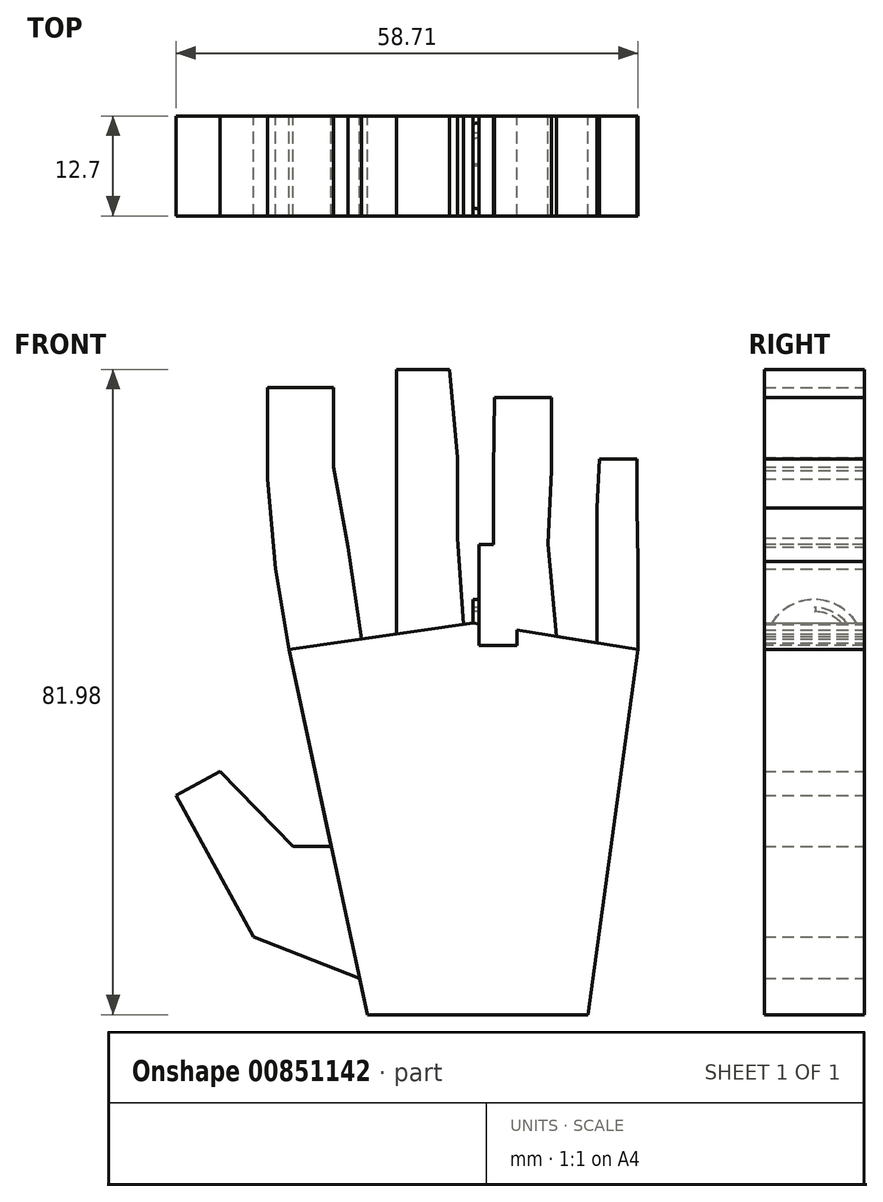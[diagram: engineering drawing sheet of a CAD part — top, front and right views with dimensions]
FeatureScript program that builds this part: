
annotation { "Feature Type Name" : "Feature", "Feature Type Description" : "" }
export const myFeature = defineFeature(function(context is Context, id is Id, definition is map)
    precondition{}
    {
        {
            var Q0;
            Q0=qCreatedBy(makeId("Front.planeOp"),FACE);
            var sketch = newSketch(context, id + "F0", { "sketchPlane" : qUnion([Q0])});
            skLineSegment(sketch, "E0", {"start": v(14.62, -41.57) * mm, "end": v(-13.4, -41.57) * mm});
            skPoint(sketch, "E1.orphan", {"position": v(0, -41.57) * mm});
            skLineSegment(sketch, "E2", {"start": v(-13.4, -41.57) * mm, "end": v(-23.39, 4.81) * mm});
            skLineSegment(sketch, "E3", {"start": v(-23.39, 4.81) * mm, "end": v(0, 8.2) * mm});
            skLineSegment(sketch, "E4", {"start": v(0, 8.2) * mm, "end": v(20.98, 4.81) * mm});
            skLineSegment(sketch, "E5", {"start": v(14.62, -41.57) * mm, "end": v(20.98, 4.81) * mm});
            skLineSegment(sketch, "E6", {"start": v(-14.4, -36.97) * mm, "end": v(-27.9, -31.67) * mm});
            skLineSegment(sketch, "E7", {"start": v(-27.9, -31.67) * mm, "end": v(-37.73, -13.72) * mm});
            skLineSegment(sketch, "E8", {"start": v(-37.73, -13.72) * mm, "end": v(-32.12, -10.65) * mm});
            skLineSegment(sketch, "E9", {"start": v(-32.12, -10.65) * mm, "end": v(-22.87, -20.16) * mm});
            skLineSegment(sketch, "E10", {"start": v(-22.87, -20.16) * mm, "end": v(-18.01, -20.16) * mm});
            skLineSegment(sketch, "E11", {"start": v(-23.39, 4.81) * mm, "end": v(-25.12, 15.03) * mm});
            skLineSegment(sketch, "E12", {"start": v(-25.12, 15.03) * mm, "end": v(-26.13, 26.5) * mm});
            skLineSegment(sketch, "E13", {"start": v(-26.13, 26.5) * mm, "end": v(-26.13, 38.07) * mm});
            skLineSegment(sketch, "E14", {"start": v(-26.13, 38.07) * mm, "end": v(-17.7, 38.07) * mm});
            skLineSegment(sketch, "E15", {"start": v(-17.7, 38.07) * mm, "end": v(-17.7, 28.01) * mm});
            skLineSegment(sketch, "E16", {"start": v(-17.7, 28.01) * mm, "end": v(-26.13, 26.5) * mm});
            skLineSegment(sketch, "E17", {"start": v(-17.7, 28.01) * mm, "end": v(-15.87, 17.87) * mm});
            skLineSegment(sketch, "E18", {"start": v(-15.87, 17.87) * mm, "end": v(-25.12, 15.03) * mm});
            skLineSegment(sketch, "E19", {"start": v(-15.87, 17.87) * mm, "end": v(-14.17, 6.15) * mm});
            skLineSegment(sketch, "E20", {"start": v(-9.7, 6.8) * mm, "end": v(-9.7, 18.15) * mm});
            skLineSegment(sketch, "E21", {"start": v(-9.7, 18.15) * mm, "end": v(-9.7, 29.23) * mm});
            skLineSegment(sketch, "E22", {"start": v(-9.7, 29.23) * mm, "end": v(-1.96, 29.23) * mm});
            skLineSegment(sketch, "E23", {"start": v(-1.96, 29.23) * mm, "end": v(-1.96, 18.96) * mm});
            skLineSegment(sketch, "E24", {"start": v(-1.96, 18.96) * mm, "end": v(-1.21, 8.03) * mm});
            skLineSegment(sketch, "E25", {"start": v(-9.7, 29.23) * mm, "end": v(-9.7, 40.4) * mm});
            skLineSegment(sketch, "E26", {"start": v(-9.7, 40.4) * mm, "end": v(-3.03, 40.4) * mm});
            skLineSegment(sketch, "E27", {"start": v(-3.03, 40.4) * mm, "end": v(-1.96, 29.23) * mm});
            skLineSegment(sketch, "E28", {"start": v(-9.7, 18.15) * mm, "end": v(-1.96, 18.96) * mm});
            skLineSegment(sketch, "E29", {"start": v(2.62, 7.78) * mm, "end": v(2.62, 18.22) * mm});
            skLineSegment(sketch, "E30", {"start": v(2.62, 18.22) * mm, "end": v(9.49, 18.22) * mm});
            skLineSegment(sketch, "E31", {"start": v(9.49, 18.22) * mm, "end": v(10.58, 6.5) * mm});
            skLineSegment(sketch, "E32", {"start": v(10.58, 6.5) * mm, "end": v(9.49, 18.22) * mm});
            skLineSegment(sketch, "E33", {"start": v(2.62, 18.22) * mm, "end": v(2.62, 27.54) * mm});
            skLineSegment(sketch, "E34", {"start": v(2.62, 27.54) * mm, "end": v(9.95, 27.54) * mm});
            skLineSegment(sketch, "E35", {"start": v(9.95, 27.54) * mm, "end": v(9.49, 18.22) * mm});
            skLineSegment(sketch, "E36", {"start": v(9.95, 27.54) * mm, "end": v(9.95, 36.85) * mm});
            skLineSegment(sketch, "E37", {"start": v(9.95, 36.85) * mm, "end": v(2.7, 36.85) * mm});
            skLineSegment(sketch, "E38", {"start": v(2.7, 36.85) * mm, "end": v(2.62, 27.54) * mm});
            skLineSegment(sketch, "E39", {"start": v(20.98, 4.81) * mm, "end": v(20.98, 15.98) * mm});
            skLineSegment(sketch, "E40", {"start": v(20.98, 15.98) * mm, "end": v(15.71, 15.98) * mm});
            skLineSegment(sketch, "E41", {"start": v(15.71, 15.98) * mm, "end": v(15.71, 5.66) * mm});
            skLineSegment(sketch, "E42", {"start": v(15.71, 15.98) * mm, "end": v(15.71, 22.79) * mm});
            skLineSegment(sketch, "E43", {"start": v(15.71, 22.79) * mm, "end": v(20.79, 22.79) * mm});
            skLineSegment(sketch, "E44", {"start": v(20.79, 22.79) * mm, "end": v(20.98, 15.98) * mm});
            skLineSegment(sketch, "E45", {"start": v(20.79, 22.79) * mm, "end": v(20.79, 29.03) * mm});
            skLineSegment(sketch, "E46", {"start": v(20.79, 29.03) * mm, "end": v(16.05, 29.03) * mm});
            skLineSegment(sketch, "E47", {"start": v(16.05, 29.03) * mm, "end": v(15.71, 22.79) * mm});
            skLineSegment(sketch, "E48", {"start": v(-18.77, 5.48) * mm, "end": v(-9.34, -41.57) * mm, "construction": true});
            skLineSegment(sketch, "E49", {"start": v(-5.64, 7.38) * mm, "end": v(-4.1, -41.57) * mm, "construction": true});
            skLineSegment(sketch, "E50", {"start": v(6.52, 7.15) * mm, "end": v(4.6, -41.57) * mm, "construction": true});
            skLineSegment(sketch, "E51", {"start": v(18.1, 5.28) * mm, "end": v(11.7, -41.57) * mm, "construction": true});
            skSolve(sketch);
        }
        {
            var Q0;
            Q0 = qSketchRegion(id + "F0", true);
            extrude(context, id + "F1", {"entities" : qUnion([Q0]), "endBound" : BoundingType.SYMMETRIC, "depth" : 12.7 * mm, "offsetDistance" : 25.4 * mm});
        }
        {
            var Q0;
            Q0=qCreatedBy(makeId("Front.planeOp"),FACE);
            var sketch = newSketch(context, id + "F2", { "sketchPlane" : qUnion([Q0])});
            skLineSegment(sketch, "E52.0", {"start": v(-13.4, -41.57) * mm, "end": v(-23.39, 4.81) * mm});
            skLineSegment(sketch, "E53.0", {"start": v(14.62, -41.57) * mm, "end": v(-13.4, -41.57) * mm});
            skLineSegment(sketch, "E54.0", {"start": v(14.62, -41.57) * mm, "end": v(20.98, 4.81) * mm});
            skLineSegment(sketch, "E55.0", {"start": v(0, 8.2) * mm, "end": v(20.98, 4.81) * mm});
            skLineSegment(sketch, "E56.0", {"start": v(-23.39, 4.81) * mm, "end": v(0, 8.2) * mm});
            skSolve(sketch);
        }
        {
            var Q0;
            Q0 = qSketchRegion(id + "F2", true);
            extrude(context, id + "F3", {"entities" : qUnion([Q0]), "endBound" : BoundingType.SYMMETRIC, "depth" : 12.7 * mm, "offsetDistance" : 25.4 * mm});
        }
        {
            var Q0;
            Q0=qCreatedBy(makeId("Right.planeOp"),FACE);
            var sketch = newSketch(context, id + "F4", { "sketchPlane" : qUnion([Q0])});
            skLineSegment(sketch, "E57", {"start": v(6.35, 4.81) * mm, "end": v(-6.35, 4.81) * mm});
            skPoint(sketch, "E58.orphan", {"position": v(0, 4.81) * mm});
            skArc(sketch, "E59", {"start": v(6.35, 4.81) * mm, "mid": v(0, 11.16) * mm, "end": v(-6.35, 4.81) * mm});
            skArc(sketch, "E60", {"start": v(5.33, 4.81) * mm, "mid": v(3.77, 8.58) * mm, "end": v(0, 10.15) * mm});
            skArc(sketch, "E61", {"start": v(4.83, 4.81) * mm, "mid": v(3.41, 8.23) * mm, "end": v(0, 9.64) * mm});
            skArc(sketch, "E62", {"start": v(0, 10.15) * mm, "mid": v(-0.25, 9.9) * mm, "end": v(0, 9.64) * mm});
            skLineSegment(sketch, "E63", {"start": v(-6.33, 5.32) * mm, "end": v(6.33, 5.32) * mm});
            skPoint(sketch, "E64.orphan", {"position": v(0, 5.32) * mm});
            skSolve(sketch);
        }
        {
            var Q0;
            {var subQ0=sQuery(id+"F4.wireOp",EDGE,"E59");var subQ1=sQuery(id+"F4.wireOp",EDGE,"E57");var subQ2=makeQuery(id+"F4.imprint","INTERSECT",VERTEX,{"disambiguationData":[OD(1.0)],"derivedFrom":[subQ1,subQ0]});Q0=makeQuery(id+"F4.imprint","IMPRINT",FACE,{"disambiguationData":[TD([[makeQuery(id+"F4.imprint","IMPRINT",EDGE,{"disambiguationData":[TD([[subQ2,1.0]])],"derivedFrom":subQ1}),-1.0]])]});}
            var Q1;
            {var subQ0=sQuery(id+"F4.wireOp",EDGE,"E60");var subQ1=sQuery(id+"F4.wireOp",EDGE,"E57");var subQ2=makeQuery(id+"F4.imprint","INTERSECT",VERTEX,{"derivedFrom":[subQ1,subQ0]});Q1=makeQuery(id+"F4.imprint","IMPRINT",FACE,{"disambiguationData":[TD([[makeQuery(id+"F4.imprint","IMPRINT",EDGE,{"disambiguationData":[TD([[subQ2,-1.0]])],"derivedFrom":subQ1}),-1.0]])]});}
            var Q2;
            {var subQ0=sQuery(id+"F4.wireOp",EDGE,"E59");var subQ1=sQuery(id+"F4.wireOp",EDGE,"E57");var subQ2=makeQuery(id+"F4.imprint","INTERSECT",VERTEX,{"disambiguationData":[OD(0.0)],"derivedFrom":[subQ1,subQ0]});Q2=makeQuery(id+"F4.imprint","IMPRINT",FACE,{"disambiguationData":[TD([[makeQuery(id+"F4.imprint","IMPRINT",EDGE,{"disambiguationData":[TD([[subQ2,-1.0]])],"derivedFrom":subQ1}),-1.0]])]});}
            var Q3;
            {var subQ0=sQuery(id+"F4.wireOp",EDGE,"E62");Q3=makeQuery(id+"F4.imprint","IMPRINT",FACE,{"disambiguationData":[TD([[makeQuery(id+"F4.imprint","IMPRINT",EDGE,{"derivedFrom":subQ0}),-1.0]])]});}
            extrude(context, id + "F5", {"entities" : qUnion([Q0, Q1, Q2, Q3]), "depth" : 6.35 * mm, "offsetDistance" : 25.4 * mm});
        }
        {
            var Q0;
            Q0=qCreatedBy(makeId("Front.planeOp"),FACE);
            var sketch = newSketch(context, id + "F6", { "sketchPlane" : qUnion([Q0])});
            skLineSegment(sketch, "E65.bottom", {"start": v(5.59, 5.32) * mm, "end": v(0.76, 5.32) * mm});
            skLineSegment(sketch, "E65.top", {"start": v(5.59, 11.97) * mm, "end": v(0.76, 11.97) * mm});
            skLineSegment(sketch, "E65.left", {"start": v(5.59, 5.32) * mm, "end": v(5.59, 11.97) * mm});
            skLineSegment(sketch, "E65.right", {"start": v(0.76, 5.32) * mm, "end": v(0.76, 11.97) * mm});
            skSolve(sketch);
        }
        {
            var Q0;
            Q0 = qSketchRegion(id + "F6", true);
            extrude(context, id + "F7", {"entities" : qUnion([Q0]), "operationType" : NewBodyOperationType.REMOVE, "endBound" : BoundingType.THROUGH_ALL, "oppositeDirection" : true, "depth" : 25.4 * mm, "offsetDistance" : 25.4 * mm, "hasSecondDirection" : true, "secondDirectionBound" : SecondDirectionBoundingType.THROUGH_ALL, "secondDirectionOppositeDirection" : false, "secondDirectionDepth" : 25.4 * mm});
        }
        {
            var Q0;
            Q0=qCreatedBy(makeId("Front.planeOp"),FACE);
            var sketch = newSketch(context, id + "F8", { "sketchPlane" : qUnion([Q0])});
            skLineSegment(sketch, "E66", {"start": v(5.59, 5.32) * mm, "end": v(0.76, 5.32) * mm});
            skLineSegment(sketch, "E67", {"start": v(0.76, 5.32) * mm, "end": v(0.76, 18.15) * mm});
            skLineSegment(sketch, "E68", {"start": v(5.59, 5.32) * mm, "end": v(5.59, 18.15) * mm});
            skLineSegment(sketch, "E69", {"start": v(5.59, 18.15) * mm, "end": v(0.76, 18.15) * mm});
            skLineSegment(sketch, "E70", {"start": v(0.76, 10.15) * mm, "end": v(0, 10.15) * mm});
            skLineSegment(sketch, "E71", {"start": v(0.76, 9.64) * mm, "end": v(0, 9.64) * mm});
            skLineSegment(sketch, "E72", {"start": v(0, 9.64) * mm, "end": v(0, 10.15) * mm});
            skLineSegment(sketch, "E73", {"start": v(5.59, 10.15) * mm, "end": v(6.35, 10.15) * mm});
            skLineSegment(sketch, "E74", {"start": v(6.35, 10.15) * mm, "end": v(6.35, 9.64) * mm});
            skLineSegment(sketch, "E75", {"start": v(6.35, 9.64) * mm, "end": v(5.59, 9.64) * mm});
            skLineSegment(sketch, "E76", {"start": v(0, 9.9) * mm, "end": v(0.76, 9.9) * mm});
            skLineSegment(sketch, "E77", {"start": v(6.35, 9.9) * mm, "end": v(5.59, 9.9) * mm});
            skSolve(sketch);
        }
        {
            var Q0;
            {var subQ4=sQuery(id+"F8.wireOp",EDGE,"E66");Q0=makeQuery(id+"F8.imprint","IMPRINT",FACE,{"disambiguationData":[TD([[makeQuery(id+"F8.imprint","IMPRINT",EDGE,{"derivedFrom":subQ4}),-1.0]])]});}
            extrude(context, id + "F9", {"entities" : qUnion([Q0]), "endBound" : BoundingType.SYMMETRIC, "depth" : 12.7 * mm, "offsetDistance" : 25.4 * mm});
        }
        {
            var Q0;
            {var subQ0=sQuery(id+"F8.wireOp",EDGE,"E73");Q0=makeQuery(id+"F8.imprint","IMPRINT",FACE,{"disambiguationData":[TD([[makeQuery(id+"F8.imprint","IMPRINT",EDGE,{"derivedFrom":subQ0}),-1.0]])]});}
            var Q1;
            Q1=sQuery(id+"F8.wireOp",EDGE,"E77");
            revolve(context, id + "F10", {"operationType" : NewBodyOperationType.ADD, "surfaceOperationType" : NewSurfaceOperationType.NEW, "entities" : qUnion([Q0]), "axis" : qUnion([Q1]), "revolveType" : RevolveType.FULL});
        }
        {
            var Q0;
            {var subQ0=sQuery(id+"F8.wireOp",EDGE,"E70");Q0=makeQuery(id+"F8.imprint","IMPRINT",FACE,{"disambiguationData":[TD([[makeQuery(id+"F8.imprint","IMPRINT",EDGE,{"derivedFrom":subQ0}),1.0]])]});}
            var Q1;
            Q1=sQuery(id+"F8.wireOp",EDGE,"E76");
            revolve(context, id + "F11", {"operationType" : NewBodyOperationType.ADD, "surfaceOperationType" : NewSurfaceOperationType.NEW, "entities" : qUnion([Q0]), "axis" : qUnion([Q1]), "revolveType" : RevolveType.FULL});
        }
    });
